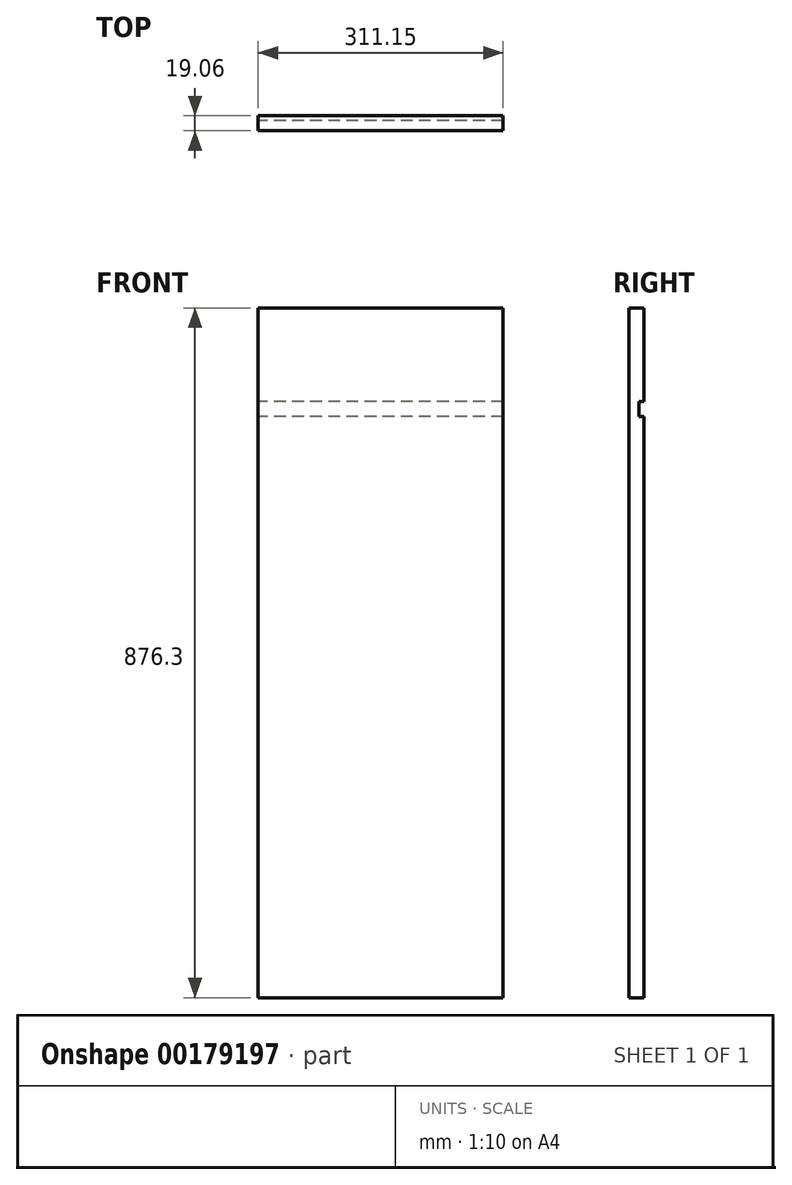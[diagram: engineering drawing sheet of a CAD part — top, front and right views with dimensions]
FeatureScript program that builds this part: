
annotation { "Feature Type Name" : "Feature", "Feature Type Description" : "" }
export const myFeature = defineFeature(function(context is Context, id is Id, definition is map)
    precondition{}
    {
        {
            var Q0;
            Q0=qCreatedBy(makeId("Front.planeOp"),FACE);
            var sketch = newSketch(context, id + "F0", { "sketchPlane" : qUnion([Q0])});
            skLineSegment(sketch, "E0.bottom", {"start": v(-247.9, 438.15) * mm, "end": v(63.25, 438.15) * mm});
            skLineSegment(sketch, "E0.top", {"start": v(-247.9, -438.15) * mm, "end": v(63.25, -438.15) * mm});
            skLineSegment(sketch, "E0.left", {"start": v(-247.9, 438.15) * mm, "end": v(-247.9, -438.15) * mm});
            skLineSegment(sketch, "E0.right", {"start": v(63.25, 438.15) * mm, "end": v(63.25, -438.15) * mm});
            skLineSegment(sketch, "E1", {"start": v(-247.9, 0) * mm, "end": v(63.25, 0) * mm});
            skSolve(sketch);
        }
        {
            var Q0;
            {var subQ0=sQuery(id+"F0.wireOp",EDGE,"E0.bottom");Q0=makeQuery(id+"F0.imprint","IMPRINT",FACE,{"disambiguationData":[TD([[makeQuery(id+"F0.imprint","IMPRINT",EDGE,{"derivedFrom":subQ0}),-1.0]])]});}
            var Q1;
            {var subQ0=sQuery(id+"F0.wireOp",EDGE,"E0.top");Q1=makeQuery(id+"F0.imprint","IMPRINT",FACE,{"disambiguationData":[TD([[makeQuery(id+"F0.imprint","IMPRINT",EDGE,{"derivedFrom":subQ0}),1.0]])]});}
            extrude(context, id + "F1", {"entities" : qUnion([Q0, Q1]), "depth" : 19.05 * mm, "symmetric" : true});
        }
        {
            var Q0;
            Q0=makeQuery(id+"F1.opExtrude","CAP_FACE",FACE,{"disambiguationData":[OSD([sQuery(id+"F0.wireOp",EDGE,"E0.bottom"),sQuery(id+"F0.wireOp",EDGE,"E0.top"),sQuery(id+"F0.wireOp",EDGE,"E0.left"),sQuery(id+"F0.wireOp",EDGE,"E0.right")])],"isStart":true});
            var sketch = newSketch(context, id + "F2", { "sketchPlane" : qUnion([Q0])});
            skLineSegment(sketch, "E2.bottom", {"start": v(-63.25, 300.04) * mm, "end": v(247.9, 300.04) * mm});
            skLineSegment(sketch, "E2.top", {"start": v(-63.25, 319.09) * mm, "end": v(247.9, 319.09) * mm});
            skLineSegment(sketch, "E2.left", {"start": v(-63.25, 300.04) * mm, "end": v(-63.25, 319.09) * mm});
            skLineSegment(sketch, "E2.right", {"start": v(247.9, 300.04) * mm, "end": v(247.9, 319.09) * mm});
            skSolve(sketch);
        }
        {
            var Q0;
            Q0=makeQuery(id+"F2.imprint","IMPRINT",FACE,{"disambiguationData":[TD([[makeQuery(id+"F2.imprint","IMPRINT",EDGE,{"derivedFrom":sQuery(id+"F2.wireOp",EDGE,"E2.bottom")}),1.0]])]});
            extrude(context, id + "F3", {"entities" : qUnion([Q0]), "operationType" : NewBodyOperationType.REMOVE, "oppositeDirection" : true, "depth" : 6.35 * mm});
        }
    });
